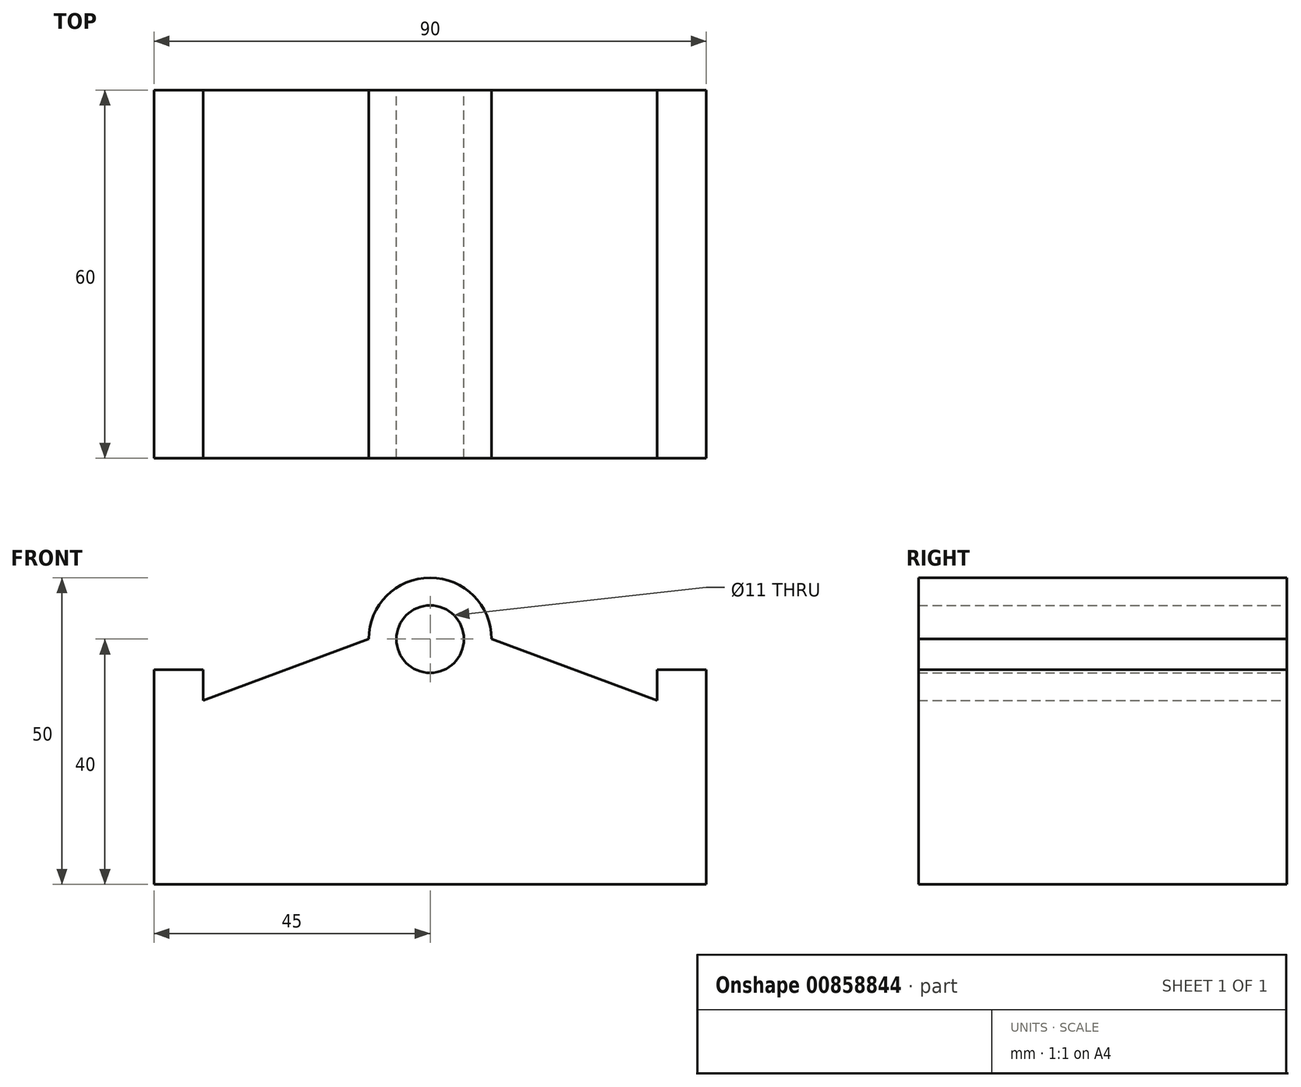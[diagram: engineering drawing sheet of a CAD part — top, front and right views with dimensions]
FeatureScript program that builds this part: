
annotation { "Feature Type Name" : "Feature", "Feature Type Description" : "" }
export const myFeature = defineFeature(function(context is Context, id is Id, definition is map)
    precondition{}
    {
        {
            var Q0;
            Q0=qCreatedBy(makeId("Front.planeOp"),FACE);
            var sketch = newSketch(context, id + "F0", { "sketchPlane" : qUnion([Q0])});
            skLineSegment(sketch, "E0", {"start": v(-45, 0) * mm, "end": v(0, 0) * mm});
            skLineSegment(sketch, "E1", {"start": v(0, 0) * mm, "end": v(45, 0) * mm});
            skLineSegment(sketch, "E2", {"start": v(45, 0) * mm, "end": v(45, 35) * mm});
            skLineSegment(sketch, "E3", {"start": v(-45, 0) * mm, "end": v(-45, 35) * mm});
            skLineSegment(sketch, "E4", {"start": v(-45, 35) * mm, "end": v(-37, 35) * mm});
            skLineSegment(sketch, "E5", {"start": v(-37, 35) * mm, "end": v(-37, 8) * mm});
            skLineSegment(sketch, "E6", {"start": v(-37, 8) * mm, "end": v(37, 8) * mm});
            skLineSegment(sketch, "E7", {"start": v(37, 8) * mm, "end": v(37, 35) * mm});
            skLineSegment(sketch, "E8", {"start": v(37, 35) * mm, "end": v(45, 35) * mm});
            skLineSegment(sketch, "E9", {"start": v(-4, 8) * mm, "end": v(4, 8) * mm});
            skLineSegment(sketch, "E10", {"start": v(4, 8) * mm, "end": v(4, 30.83) * mm});
            skLineSegment(sketch, "E11", {"start": v(-4, 8) * mm, "end": v(-4, 30.83) * mm});
            skArc(sketch, "E12", {"start": v(4, 30.83) * mm, "mid": v(0, 50) * mm, "end": v(-4, 30.83) * mm});
            skCircle(sketch, "E13", {"center": v(0, 40) * mm, "radius": 5.5 * mm});
            skLineSegment(sketch, "E14", {"start": v(-37, 30) * mm, "end": v(-10, 40) * mm});
            skLineSegment(sketch, "E15", {"start": v(10, 40) * mm, "end": v(37, 30) * mm});
            skSolve(sketch);
        }
        {
            var Q0;
            Q0 = qSketchRegion(id + "F0", true);
            extrude(context, id + "F1", {"entities" : qUnion([Q0]), "depth" : 60 * mm, "offsetDistance" : 25 * mm});
        }
    });
